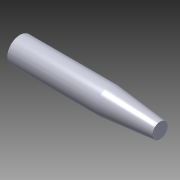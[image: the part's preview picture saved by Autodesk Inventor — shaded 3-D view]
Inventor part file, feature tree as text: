
AUTODESK INVENTOR PART (.ipt)
format: ipt  version: 2016 (Build 200138000, 138)  size: 109,056 bytes
history: native  units: in
note: dims shown in document units (in); Inventor stores cm internally (conversion verified against a paired STEP export)
features: revolve x1, other x1, imported_body x1
ambient origin geometry x8: Origin, YZ Plane, XZ Plane, XY Plane, X Axis, Y Axis, Z Axis, Center Point
bodies: Body1 (feature_tree)
feature tree (3):
  revolve  "Revolve1"  [1 undecoded]
  other  "Platen1"
  imported_body  "Base1"
note: 1 required parameter value undecoded (feature->parameter linkage not recoverable at this tier; creation-order binding heuristic only, values carry confidence <= 0.55)
